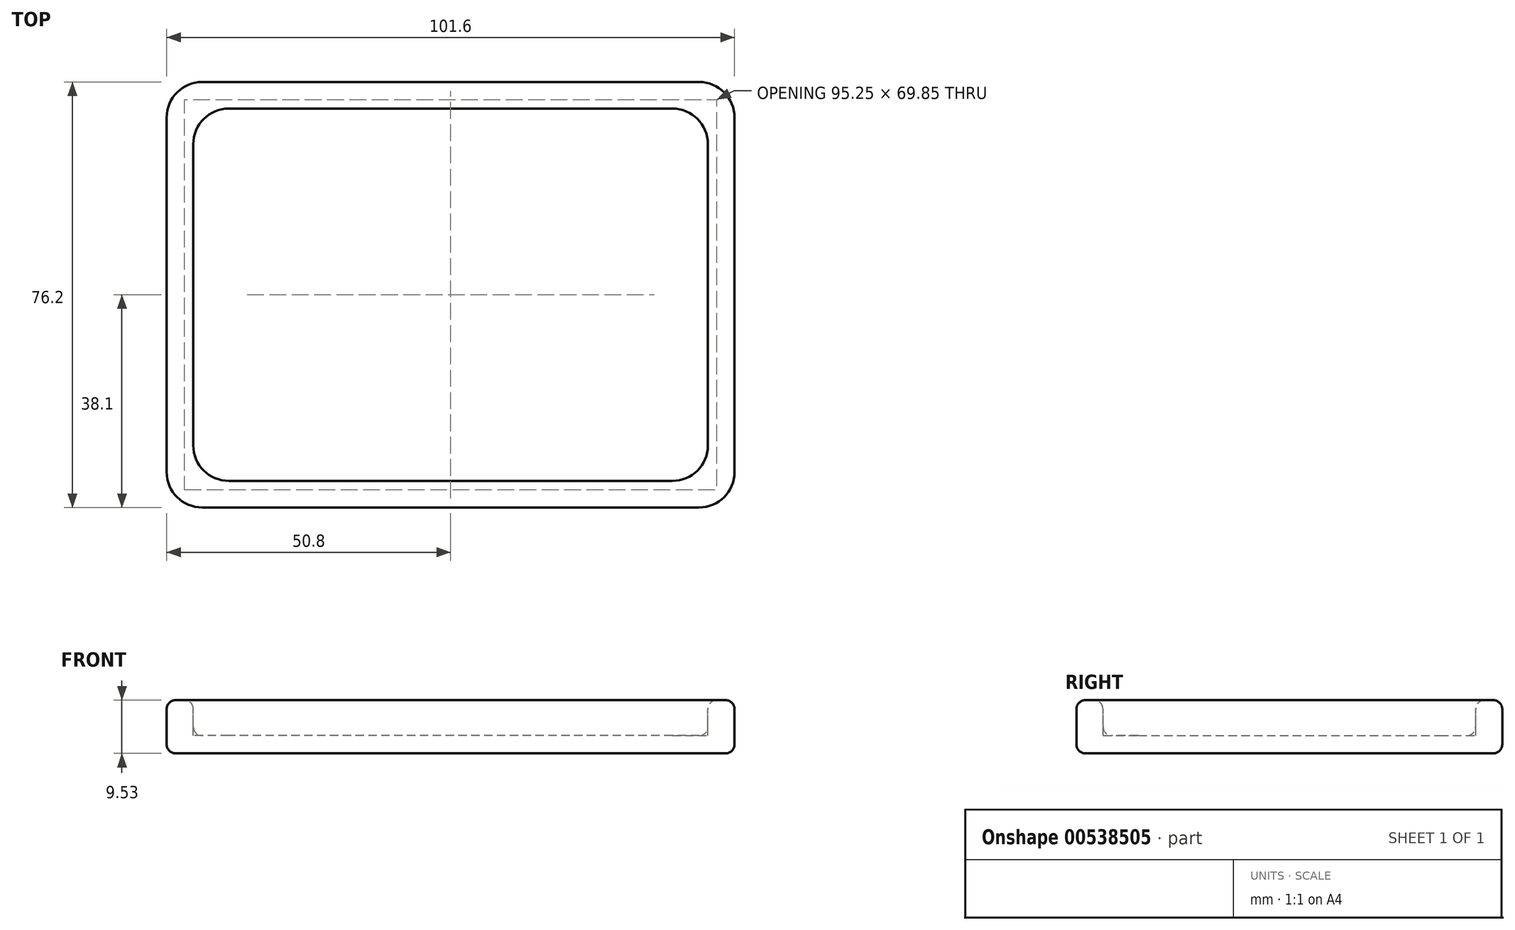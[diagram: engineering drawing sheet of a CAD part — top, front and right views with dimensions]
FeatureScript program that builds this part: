
annotation { "Feature Type Name" : "Feature", "Feature Type Description" : "" }
export const myFeature = defineFeature(function(context is Context, id is Id, definition is map)
    precondition{}
    {
        {
            var Q0;
            Q0=qCreatedBy(makeId("Top.planeOp"),FACE);
            var sketch = newSketch(context, id + "F0", { "sketchPlane" : qUnion([Q0])});
            skLineSegment(sketch, "E0.bottom", {"start": v(6.35, 0) * mm, "end": v(95.25, 0) * mm});
            skLineSegment(sketch, "E0.top", {"start": v(6.35, 76.2) * mm, "end": v(95.25, 76.2) * mm});
            skLineSegment(sketch, "E0.left", {"start": v(0, 6.35) * mm, "end": v(0, 69.85) * mm});
            skLineSegment(sketch, "E0.right", {"start": v(101.6, 6.35) * mm, "end": v(101.6, 69.85) * mm});
            skPoint(sketch, "E1.visualSharp", {"position": v(0, 76.2) * mm});
            skArc(sketch, "E1.filletArc", {"start": v(6.35, 76.2) * mm, "mid": v(1.86, 74.34) * mm, "end": v(0, 69.85) * mm});
            skPoint(sketch, "E2.visualSharp", {"position": v(101.6, 76.2) * mm});
            skArc(sketch, "E2.filletArc", {"start": v(101.6, 69.85) * mm, "mid": v(99.74, 74.34) * mm, "end": v(95.25, 76.2) * mm});
            skPoint(sketch, "E3.visualSharp", {"position": v(101.6, 0) * mm});
            skArc(sketch, "E3.filletArc", {"start": v(95.25, 0) * mm, "mid": v(99.74, 1.86) * mm, "end": v(101.6, 6.35) * mm});
            skPoint(sketch, "E4.visualSharp", {"position": v(0, 0) * mm});
            skArc(sketch, "E4.filletArc", {"start": v(0, 6.35) * mm, "mid": v(1.86, 1.86) * mm, "end": v(6.35, 0) * mm});
            skSolve(sketch);
        }
        {
            var Q0;
            Q0 = qSketchRegion(id + "F0", true);
            extrude(context, id + "F1", {"entities" : qUnion([Q0]), "depth" : 9.52 * mm, "offsetDistance" : 25.4 * mm});
        }
        {
            var Q0;
            Q0=makeQuery(id+"F1.opExtrude","CAP_FACE",FACE,{"disambiguationData":[OSD([sQuery(id+"F0.wireOp",EDGE,"E0.bottom"),sQuery(id+"F0.wireOp",EDGE,"E0.top"),sQuery(id+"F0.wireOp",EDGE,"E0.left"),sQuery(id+"F0.wireOp",EDGE,"E0.right"),sQuery(id+"F0.wireOp",EDGE,"E1.filletArc"),sQuery(id+"F0.wireOp",EDGE,"E2.filletArc"),sQuery(id+"F0.wireOp",EDGE,"E3.filletArc"),sQuery(id+"F0.wireOp",EDGE,"E4.filletArc")])],"isStart":false});
            var sketch = newSketch(context, id + "F2", { "sketchPlane" : qUnion([Q0])});
            skLineSegment(sketch, "E5.0", {"start": v(90.49, 71.44) * mm, "end": v(11.11, 71.44) * mm});
            skLineSegment(sketch, "E5.1", {"start": v(96.84, 11.11) * mm, "end": v(96.84, 65.09) * mm});
            skLineSegment(sketch, "E5.2", {"start": v(11.11, 4.76) * mm, "end": v(90.49, 4.76) * mm});
            skLineSegment(sketch, "E5.3", {"start": v(4.76, 65.09) * mm, "end": v(4.76, 11.11) * mm});
            skPoint(sketch, "E6.visualSharp", {"position": v(96.84, 71.44) * mm});
            skArc(sketch, "E6.filletArc", {"start": v(96.84, 65.09) * mm, "mid": v(94.98, 69.58) * mm, "end": v(90.49, 71.44) * mm});
            skPoint(sketch, "E7.visualSharp", {"position": v(96.84, 4.76) * mm});
            skArc(sketch, "E7.filletArc", {"start": v(90.49, 4.76) * mm, "mid": v(94.98, 6.62) * mm, "end": v(96.84, 11.11) * mm});
            skPoint(sketch, "E8.visualSharp", {"position": v(4.76, 4.76) * mm});
            skArc(sketch, "E8.filletArc", {"start": v(4.76, 11.11) * mm, "mid": v(6.62, 6.62) * mm, "end": v(11.11, 4.76) * mm});
            skPoint(sketch, "E9.visualSharp", {"position": v(4.76, 71.44) * mm});
            skArc(sketch, "E9.filletArc", {"start": v(11.11, 71.44) * mm, "mid": v(6.62, 69.58) * mm, "end": v(4.76, 65.09) * mm});
            skSolve(sketch);
        }
        {
            var Q0;
            Q0=makeQuery(id+"F2.imprint","IMPRINT",FACE,{"disambiguationData":[TD([[makeQuery(id+"F2.imprint","IMPRINT",EDGE,{"derivedFrom":sQuery(id+"F2.wireOp",EDGE,"E5.0")}),1.0]])]});
            extrude(context, id + "F3", {"entities" : qUnion([Q0]), "operationType" : NewBodyOperationType.REMOVE, "oppositeDirection" : true, "depth" : 6.35 * mm, "offsetDistance" : 25.4 * mm});
        }
        {
            var Q0;
            Q0=makeQuery(id+"F1.opExtrude","CAP_FACE",FACE,{"disambiguationData":[OSD([sQuery(id+"F0.wireOp",EDGE,"E0.bottom"),sQuery(id+"F0.wireOp",EDGE,"E0.top"),sQuery(id+"F0.wireOp",EDGE,"E0.left"),sQuery(id+"F0.wireOp",EDGE,"E0.right"),sQuery(id+"F0.wireOp",EDGE,"E1.filletArc"),sQuery(id+"F0.wireOp",EDGE,"E2.filletArc"),sQuery(id+"F0.wireOp",EDGE,"E3.filletArc"),sQuery(id+"F0.wireOp",EDGE,"E4.filletArc")])],"isStart":false});
            var Q1;
            Q1=makeQuery(id+"F1.opExtrude","CAP_FACE",FACE,{"disambiguationData":[OSD([sQuery(id+"F0.wireOp",EDGE,"E0.bottom"),sQuery(id+"F0.wireOp",EDGE,"E0.top"),sQuery(id+"F0.wireOp",EDGE,"E0.left"),sQuery(id+"F0.wireOp",EDGE,"E0.right"),sQuery(id+"F0.wireOp",EDGE,"E1.filletArc"),sQuery(id+"F0.wireOp",EDGE,"E2.filletArc"),sQuery(id+"F0.wireOp",EDGE,"E3.filletArc"),sQuery(id+"F0.wireOp",EDGE,"E4.filletArc")])],"isStart":true});
            fillet(context, id + "F4", {"entities" : qUnion([Q0, Q1]), "radius" : 1.59 * mm, "tangentPropagation" : true, "allowEdgeOverflow" : false});
        }
        {
            var Q0;
            Q0=makeQuery(id+"F3.boolean.opBoolean","COPY",FACE,{"derivedFrom":makeQuery(id+"F3.opExtrude","CAP_FACE",FACE,{"disambiguationData":[OSD([sQuery(id+"F2.wireOp",EDGE,"E5.0"),sQuery(id+"F2.wireOp",EDGE,"E5.1"),sQuery(id+"F2.wireOp",EDGE,"E5.2"),sQuery(id+"F2.wireOp",EDGE,"E5.3"),sQuery(id+"F2.wireOp",EDGE,"E6.filletArc"),sQuery(id+"F2.wireOp",EDGE,"E7.filletArc"),sQuery(id+"F2.wireOp",EDGE,"E8.filletArc"),sQuery(id+"F2.wireOp",EDGE,"E9.filletArc")])],"isStart":false})});
            fillet(context, id + "F5", {"entities" : qUnion([Q0]), "radius" : 1.59 * mm, "tangentPropagation" : true, "allowEdgeOverflow" : false});
        }
    });
